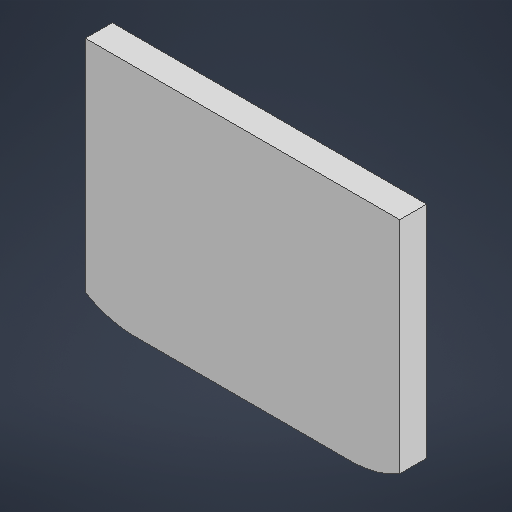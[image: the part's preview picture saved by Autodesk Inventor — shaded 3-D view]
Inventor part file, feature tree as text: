
AUTODESK INVENTOR PART (.ipt)
format: ipt  version: 2025 (Build 290162000, 162)  size: 215,040 bytes
history: native  units: mm
features: extrude x2, sketch x2, mirror x1, projected_geometry x1, plane x1
ambient origin geometry x8: Origin, YZ Plane, XZ Plane, XY Plane, X Axis, Y Axis, Z Axis, Center Point
bodies: 实体1 (feature_tree)
feature tree (7):
  extrude  "拉伸1"  Depth=52.0mm
  extrude  "拉伸2"  Depth=6.0mm
  mirror  "镜像1"
  sketch  "草图1"  dims[d0=70.0mm d1=52.0mm]
  sketch  "草图2"  dims[d2=6.0mm d3=0.0mm d4=3.0mm d5=10.0mm d6=6.0mm d7=0.0mm]
  projected_geometry  "投影回路1"
  plane  "工作平面1"
